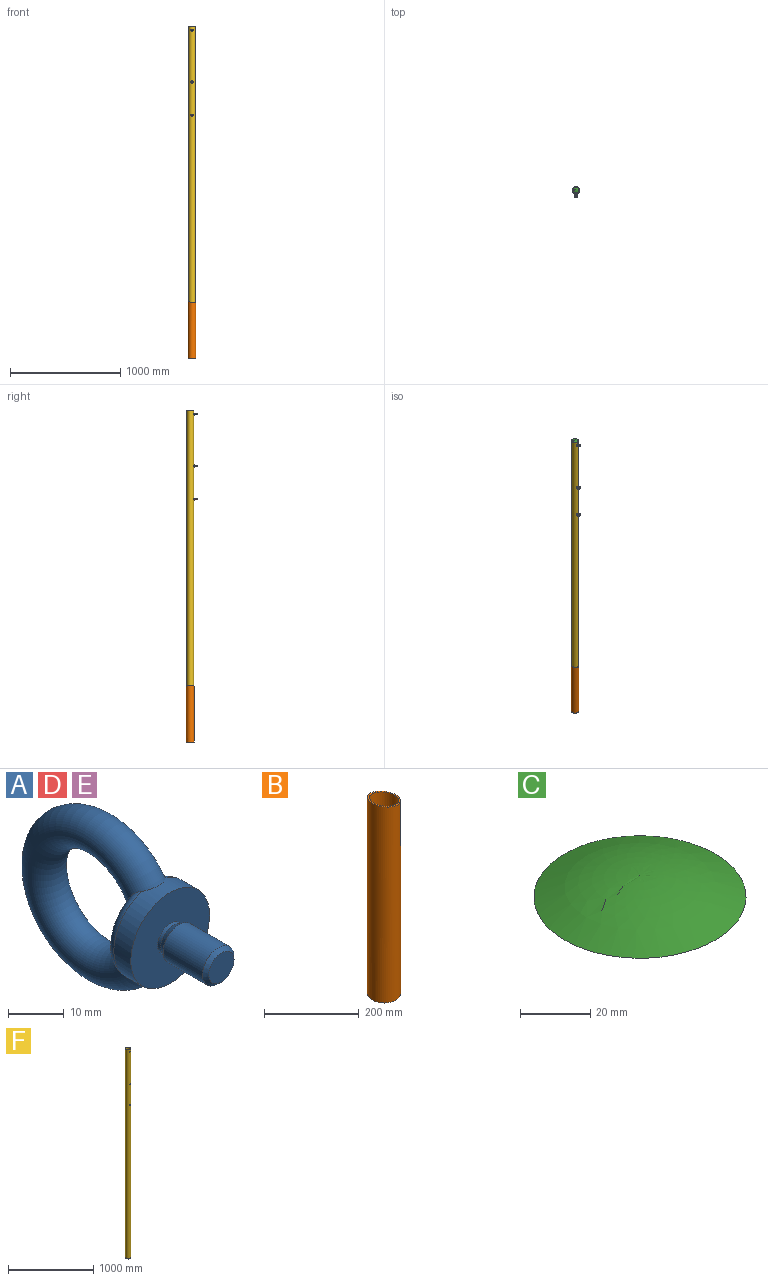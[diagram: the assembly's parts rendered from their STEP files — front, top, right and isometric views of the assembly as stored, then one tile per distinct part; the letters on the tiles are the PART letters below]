
ASSEMBLY  parts=6 mates=8
PART A: 12 faces, bbox 21.6x50.5x39 mm
  f0: cone r=0mm half-angle=78.2deg, axis (0,-1,0), area 61.8mm2, adj f1,f6
  f1: torus R=8mm, axis (0,-1,0), area 60.6mm2, adj f0,f4,f6
  f2: cone r=0mm half-angle=78.2deg, axis (0,-1,0), area 61.8mm2, adj f3,f6
  f3: torus R=8mm, axis (0,-1,0), area 60.6mm2, adj f2,f4,f6
  f4: cylinder r=10mm len=20mm, axis (0,-1,0), area 260.5mm2, adj f1,f3,f5,f6
  f5: plane 20x20mm, normal (0,-1,0), area 282mm2, adj f4,f7
  f6: torus R=14mm, axis (1,0,0), area 1882mm2, adj f0,f1,f2,f3,f4
  f7: cylinder r=3.2mm len=6.4mm, axis (0,-1,0), area 16.1mm2, adj f5,f8
  f8: cone r=3.2mm half-angle=30deg, axis (0,-1,0), area 36.2mm2, adj f7,f9
  f9: cylinder r=4mm len=10.01mm, axis (0,-1,0), area 251.7mm2, adj f8,f10
  f10: cone r=4mm half-angle=45deg, axis (0,1,0), area 25.6mm2, adj f9,f11
  f11: plane 6.4x6.4mm, normal (0,-1,0), area 32.2mm2, adj f10
PART B: 4 faces, bbox 70x70x510.1 mm
  f0: cylinder r=31mm len=509.37mm, axis (0,0,-1), area 98135.1mm2, adj f2,f3
  f1: cylinder r=35mm len=510.08mm, axis (0,0,-1), area 110797.7mm2, adj f2,f3
  f2: plane 70x70mm, normal (0,0,-1), area 829.4mm2, adj f0,f1
  f3: plane 70x70mm, normal (0.17,0,0.98), area 842.2mm2, adj f0,f1
PART C: 2 faces, bbox 180.9x180.9x120.6 mm
  f0: revolved ~60.3x30.15mm, area 0mm2, adj f1
  f1: plane 180.9x180.9mm, normal (0,0,-1), area 2855.8mm2, adj f0
PART D: same geometry as A
PART E: same geometry as A
PART F: 7 faces, bbox 60.3x60.3x3000 mm
  f0: cylinder r=27.15mm len=3000mm, axis (0,0,-1), area 511472.9mm2, adj f2,f3,f4,f5,f6
  f1: cylinder r=30.15mm len=3000mm, axis (0,0,-1), area 568021.8mm2, adj f2,f3,f4,f5,f6
  f2: plane 60.3x60.3mm, normal (0,0,1), area 540mm2, adj f0,f1
  f3: plane 60.3x60.3mm, normal (0,0,-1), area 540mm2, adj f0,f1
  f4: cylinder r=5.55mm len=11.1mm, axis (0,1,0), area 105.6mm2, adj f0,f1
  f5: cylinder r=5.55mm len=11.1mm, axis (0,1,0), area 105.6mm2, adj f0,f1
  f6: cylinder r=5.55mm len=11.1mm, axis (0,1,0), area 105.6mm2, adj f0,f1
PLACE A rot(axis=(-0.71,0,0.71),180deg) t=(0,-30.15,1470)mm
PLACE B t=(0,0,-1245)mm
PLACE C t=(0,0,1500)mm
PLACE D rot(axis=(-0.71,0,0.71),180deg) t=(0,-30.15,1000)mm
PLACE E rot(axis=(-0.71,0,0.71),180deg) t=(0,-30.15,700)mm
PLACE F at identity fixed
MATE parallel F.f1 <-> D.f6  axis (0,0,1) through (0,0,1500)mm
MATE parallel F.f1 <-> A.f6  axis (0,0,1) through (0,0,1500)mm
MATE fastened B.f1 <-> F.f1  axis (0,0,-1) through (0,0,-1500)mm
MATE fastened F.f1 <-> C.f1  axis (0,0,1) through (0,0,1500)mm
MATE parallel F.f1 <-> E.f6  axis (0,0,1) through (0,0,1500)mm
MATE cylindrical F.f5 <-> D.f0  axis (0,1,0) through (0,-28.36,1000)mm
MATE cylindrical E.f0 <-> F.f4  axis (0,1,0) through (0,-22.96,700)mm
MATE cylindrical F.f6 <-> A.f0  axis (0,1,0) through (0,-28.36,1470)mm
